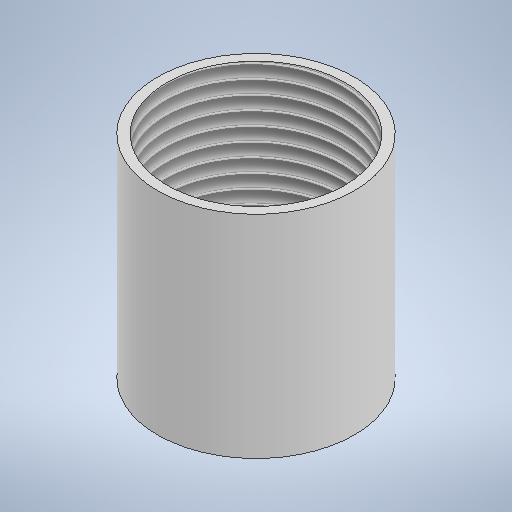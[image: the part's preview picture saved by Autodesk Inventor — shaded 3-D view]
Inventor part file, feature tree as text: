
AUTODESK INVENTOR PART (.ipt)
format: ipt  version: 2025 (Build 290162010, 162A)  size: 251,392 bytes
history: native  units: mm
features: sketch x2, extrude x1, hole x1
ambient origin geometry x8: Origin, YZ Plane, XZ Plane, XY Plane, X Axis, Y Axis, Z Axis, Center Point
bodies: Solid1 (feature_tree)
feature tree (4):
  extrude  "Extrusion1"  Depth=36.0mm TaperAngle=0.0deg
  hole  "Hole1"  [1 undecoded]
  sketch  "Sketch1"  dims[d0=33.5mm d1=36.0mm d2=0.0mm]
  sketch  "Sketch2"  dims[d3=30.291mm d4=66.498mm d5=4.0mm d6=2.0mm d7=90.0deg d8=8.0mm d9=20.594885mm]
note: 1 required parameter value undecoded (feature->parameter linkage not recoverable at this tier; creation-order binding heuristic only, values carry confidence <= 0.55)
